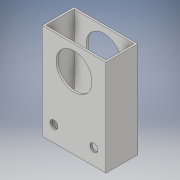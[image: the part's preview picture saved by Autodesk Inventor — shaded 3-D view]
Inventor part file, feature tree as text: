
AUTODESK INVENTOR PART (.ipt)
format: ipt  version: 2018 (Build 220112000, 112)  size: 132,608 bytes
history: native  units: in
note: dims shown in document units (in); Inventor stores cm internally (conversion verified against a paired STEP export)
features: extrude x2, sketch x2
ambient origin geometry x8: Origin, YZ Plane, XZ Plane, XY Plane, X Axis, Y Axis, Z Axis, Center Point
bodies: Body1 (feature_tree)
feature tree (4):
  extrude  "Extrusion2"  Depth=2.0in
  extrude  "Extrusion3"  Depth=0.0625in
  sketch  "Sketch1"  dims[d1=1.0in d4=2.0in]
  sketch  "Sketch2"  dims[d7=0.0625in d8=0.0625in d9=0.0625in d10=0.0625in d11=3.0in d12=0.0in d13=1.125in d14=1.25in d15=0.375in d16=0.5in d17=0.5in d18=0.75in d19=0.25in d20=0.25in d21=3.0in d22=0.0in]
